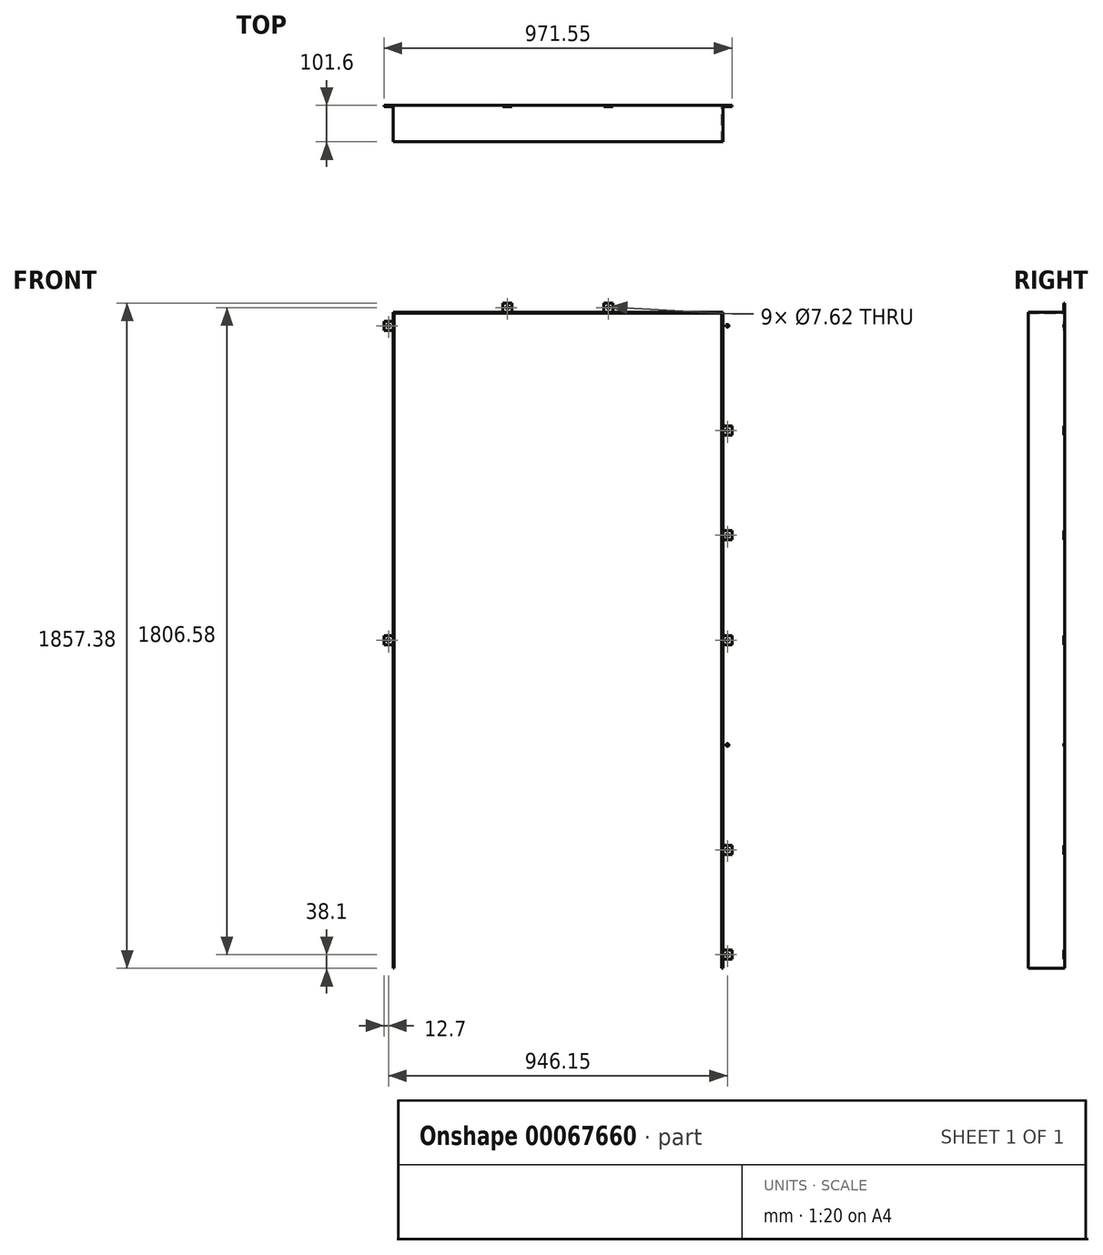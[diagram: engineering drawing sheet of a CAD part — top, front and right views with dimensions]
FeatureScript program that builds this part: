
annotation { "Feature Type Name" : "Feature", "Feature Type Description" : "" }
export const myFeature = defineFeature(function(context is Context, id is Id, definition is map)
    precondition{}
    {
        {
            var Q0;
            Q0=qCreatedBy(makeId("Front.planeOp"),FACE);
            var sketch = newSketch(context, id + "F0", { "sketchPlane" : qUnion([Q0])});
            skLineSegment(sketch, "E0", {"start": v(0, 0) * mm, "end": v(0, 1831.98) * mm});
            skLineSegment(sketch, "E1", {"start": v(0, 1831.98) * mm, "end": v(920.75, 1831.98) * mm});
            skLineSegment(sketch, "E2", {"start": v(920.75, 1831.98) * mm, "end": v(920.75, 0) * mm});
            skLineSegment(sketch, "E3", {"start": v(920.75, 0) * mm, "end": v(917.58, 0) * mm});
            skLineSegment(sketch, "E4", {"start": v(917.58, 0) * mm, "end": v(917.58, 1828.8) * mm});
            skLineSegment(sketch, "E5", {"start": v(917.58, 1828.8) * mm, "end": v(3.17, 1828.8) * mm});
            skLineSegment(sketch, "E6", {"start": v(3.18, 1828.8) * mm, "end": v(3.18, 0) * mm});
            skLineSegment(sketch, "E7", {"start": v(3.18, 0) * mm, "end": v(0, 0) * mm});
            skLineSegment(sketch, "E8", {"start": v(460.38, 1831.98) * mm, "end": v(460.38, 1828.8) * mm, "construction": true});
            skLineSegment(sketch, "E9", {"start": v(460.38, 1828.8) * mm, "end": v(460.38, -376.43) * mm, "construction": true});
            skLineSegment(sketch, "E10.bottom", {"start": v(0, 1806.57) * mm, "end": v(-25.4, 1806.57) * mm});
            skLineSegment(sketch, "E10.top", {"start": v(0, 1781.17) * mm, "end": v(-25.4, 1781.17) * mm});
            skLineSegment(sketch, "E10.left", {"start": v(0, 1806.57) * mm, "end": v(0, 1781.17) * mm});
            skLineSegment(sketch, "E10.right", {"start": v(-25.4, 1806.57) * mm, "end": v(-25.4, 1781.17) * mm});
            skLineSegment(sketch, "E11", {"start": v(-12.7, 1806.57) * mm, "end": v(-12.7, 1781.17) * mm, "construction": true});
            skLineSegment(sketch, "E12", {"start": v(-25.4, 1793.87) * mm, "end": v(0, 1793.87) * mm, "construction": true});
            skCircle(sketch, "E13", {"center": v(-12.7, 1793.87) * mm, "radius": 3.81 * mm});
            skLineSegment(sketch, "E14.left", {"start": v(0, 1513.95) * mm, "end": v(0, 1488.55) * mm});
            skLineSegment(sketch, "E15", {"start": v(-25.4, 1501.25) * mm, "end": v(0, 1501.25) * mm, "construction": true});
            skLineSegment(sketch, "E16", {"start": v(-12.7, 1513.95) * mm, "end": v(-12.7, 1488.55) * mm, "construction": true});
            skLineSegment(sketch, "E14.right", {"start": v(-25.4, 1513.95) * mm, "end": v(-25.4, 1488.55) * mm});
            skLineSegment(sketch, "E14.top", {"start": v(0, 1488.55) * mm, "end": v(-25.4, 1488.55) * mm});
            skLineSegment(sketch, "E14.bottom", {"start": v(0, 1513.95) * mm, "end": v(-25.4, 1513.95) * mm});
            skCircle(sketch, "E17", {"center": v(-12.7, 1501.25) * mm, "radius": 3.81 * mm});
            skLineSegment(sketch, "E18.left", {"start": v(0, 1221.32) * mm, "end": v(0, 1195.92) * mm});
            skLineSegment(sketch, "E19", {"start": v(-25.4, 1208.62) * mm, "end": v(0, 1208.62) * mm, "construction": true});
            skLineSegment(sketch, "E20", {"start": v(-12.7, 1221.32) * mm, "end": v(-12.7, 1195.92) * mm, "construction": true});
            skLineSegment(sketch, "E18.right", {"start": v(-25.4, 1221.32) * mm, "end": v(-25.4, 1195.92) * mm});
            skLineSegment(sketch, "E18.top", {"start": v(0, 1195.92) * mm, "end": v(-25.4, 1195.92) * mm});
            skLineSegment(sketch, "E18.bottom", {"start": v(0, 1221.32) * mm, "end": v(-25.4, 1221.32) * mm});
            skCircle(sketch, "E21", {"center": v(-12.7, 1208.62) * mm, "radius": 3.81 * mm});
            skLineSegment(sketch, "E22.left", {"start": v(0, 50.8) * mm, "end": v(0, 25.4) * mm});
            skLineSegment(sketch, "E23", {"start": v(-25.4, 38.1) * mm, "end": v(0, 38.1) * mm, "construction": true});
            skLineSegment(sketch, "E24", {"start": v(-12.7, 50.8) * mm, "end": v(-12.7, 25.4) * mm, "construction": true});
            skLineSegment(sketch, "E22.right", {"start": v(-25.4, 50.8) * mm, "end": v(-25.4, 25.4) * mm});
            skLineSegment(sketch, "E22.top", {"start": v(0, 25.4) * mm, "end": v(-25.4, 25.4) * mm});
            skLineSegment(sketch, "E22.bottom", {"start": v(0, 50.8) * mm, "end": v(-25.4, 50.8) * mm});
            skCircle(sketch, "E25", {"center": v(-12.7, 38.1) * mm, "radius": 3.81 * mm});
            skLineSegment(sketch, "E26.left", {"start": v(0, 343.43) * mm, "end": v(0, 318.03) * mm});
            skLineSegment(sketch, "E27", {"start": v(-25.4, 330.73) * mm, "end": v(0, 330.73) * mm, "construction": true});
            skLineSegment(sketch, "E28", {"start": v(-12.7, 343.43) * mm, "end": v(-12.7, 318.03) * mm, "construction": true});
            skLineSegment(sketch, "E26.right", {"start": v(-25.4, 343.43) * mm, "end": v(-25.4, 318.03) * mm});
            skLineSegment(sketch, "E26.top", {"start": v(0, 318.03) * mm, "end": v(-25.4, 318.03) * mm});
            skLineSegment(sketch, "E26.bottom", {"start": v(0, 343.43) * mm, "end": v(-25.4, 343.43) * mm});
            skCircle(sketch, "E29", {"center": v(-12.7, 330.73) * mm, "radius": 3.81 * mm});
            skLineSegment(sketch, "E30.left", {"start": v(0, 636.06) * mm, "end": v(0, 610.66) * mm});
            skLineSegment(sketch, "E31", {"start": v(-25.4, 623.36) * mm, "end": v(0, 623.36) * mm, "construction": true});
            skLineSegment(sketch, "E32", {"start": v(-12.7, 636.06) * mm, "end": v(-12.7, 610.66) * mm, "construction": true});
            skLineSegment(sketch, "E30.right", {"start": v(-25.4, 636.06) * mm, "end": v(-25.4, 610.66) * mm});
            skLineSegment(sketch, "E30.top", {"start": v(0, 610.66) * mm, "end": v(-25.4, 610.66) * mm});
            skLineSegment(sketch, "E30.bottom", {"start": v(0, 636.06) * mm, "end": v(-25.4, 636.06) * mm});
            skCircle(sketch, "E33", {"center": v(-12.7, 623.36) * mm, "radius": 3.81 * mm});
            skLineSegment(sketch, "E34.MirrorCS", {"start": v(946.15, 1793.87) * mm, "end": v(920.75, 1793.87) * mm, "construction": true});
            skCircle(sketch, "E35.MirrorC", {"center": v(933.45, 1793.88) * mm, "radius": 3.81 * mm});
            skLineSegment(sketch, "E36.MirrorCS", {"start": v(920.75, 1806.57) * mm, "end": v(946.15, 1806.57) * mm});
            skLineSegment(sketch, "E37.MirrorCS", {"start": v(933.45, 1806.58) * mm, "end": v(933.45, 1781.18) * mm, "construction": true});
            skLineSegment(sketch, "E38.MirrorCS", {"start": v(946.15, 1806.58) * mm, "end": v(946.15, 1781.18) * mm});
            skLineSegment(sketch, "E39.MirrorCS", {"start": v(920.75, 1806.58) * mm, "end": v(920.75, 1781.18) * mm});
            skLineSegment(sketch, "E40.MirrorCS", {"start": v(920.75, 1781.17) * mm, "end": v(946.15, 1781.17) * mm});
            skLineSegment(sketch, "E41.MirrorCS", {"start": v(946.15, 1501.25) * mm, "end": v(920.75, 1501.25) * mm, "construction": true});
            skLineSegment(sketch, "E42.MirrorCS", {"start": v(920.75, 1513.95) * mm, "end": v(946.15, 1513.95) * mm});
            skCircle(sketch, "E43.MirrorC", {"center": v(933.45, 1501.25) * mm, "radius": 3.81 * mm});
            skLineSegment(sketch, "E44.MirrorCS", {"start": v(920.75, 1513.95) * mm, "end": v(920.75, 1488.55) * mm});
            skLineSegment(sketch, "E45.MirrorCS", {"start": v(933.45, 1513.95) * mm, "end": v(933.45, 1488.55) * mm, "construction": true});
            skLineSegment(sketch, "E46.MirrorCS", {"start": v(946.15, 1513.95) * mm, "end": v(946.15, 1488.55) * mm});
            skLineSegment(sketch, "E47.MirrorCS", {"start": v(920.75, 1488.55) * mm, "end": v(946.15, 1488.55) * mm});
            skLineSegment(sketch, "E48.MirrorCS", {"start": v(946.15, 1221.32) * mm, "end": v(946.15, 1195.92) * mm});
            skLineSegment(sketch, "E49.MirrorCS", {"start": v(946.15, 1208.62) * mm, "end": v(920.75, 1208.62) * mm, "construction": true});
            skLineSegment(sketch, "E50.MirrorCS", {"start": v(933.45, 1221.32) * mm, "end": v(933.45, 1195.92) * mm, "construction": true});
            skCircle(sketch, "E51.MirrorC", {"center": v(933.45, 1208.62) * mm, "radius": 3.81 * mm});
            skLineSegment(sketch, "E52.MirrorCS", {"start": v(920.75, 1195.92) * mm, "end": v(946.15, 1195.92) * mm});
            skLineSegment(sketch, "E53.MirrorCS", {"start": v(920.75, 1221.32) * mm, "end": v(920.75, 1195.92) * mm});
            skLineSegment(sketch, "E54.MirrorCS", {"start": v(920.75, 1221.32) * mm, "end": v(946.15, 1221.32) * mm});
            skCircle(sketch, "E55.MirrorC", {"center": v(933.45, 623.36) * mm, "radius": 3.81 * mm});
            skLineSegment(sketch, "E56.MirrorCS", {"start": v(920.75, 636.06) * mm, "end": v(946.15, 636.06) * mm});
            skLineSegment(sketch, "E57.MirrorCS", {"start": v(946.15, 623.36) * mm, "end": v(920.75, 623.36) * mm, "construction": true});
            skLineSegment(sketch, "E58.MirrorCS", {"start": v(933.45, 636.06) * mm, "end": v(933.45, 610.66) * mm, "construction": true});
            skLineSegment(sketch, "E59.MirrorCS", {"start": v(920.75, 636.06) * mm, "end": v(920.75, 610.66) * mm});
            skLineSegment(sketch, "E60.MirrorCS", {"start": v(920.75, 610.66) * mm, "end": v(946.15, 610.66) * mm});
            skLineSegment(sketch, "E61.MirrorCS", {"start": v(946.15, 636.06) * mm, "end": v(946.15, 610.66) * mm});
            skLineSegment(sketch, "E62.MirrorCS", {"start": v(946.15, 343.43) * mm, "end": v(946.15, 318.03) * mm});
            skLineSegment(sketch, "E63.MirrorCS", {"start": v(920.75, 318.03) * mm, "end": v(946.15, 318.03) * mm});
            skLineSegment(sketch, "E64.MirrorCS", {"start": v(933.45, 343.43) * mm, "end": v(933.45, 318.03) * mm, "construction": true});
            skLineSegment(sketch, "E65.MirrorCS", {"start": v(920.75, 343.43) * mm, "end": v(946.15, 343.43) * mm});
            skLineSegment(sketch, "E66.MirrorCS", {"start": v(946.15, 330.73) * mm, "end": v(920.75, 330.73) * mm, "construction": true});
            skLineSegment(sketch, "E67.MirrorCS", {"start": v(920.75, 343.43) * mm, "end": v(920.75, 318.03) * mm});
            skCircle(sketch, "E68.MirrorC", {"center": v(933.45, 330.73) * mm, "radius": 3.81 * mm});
            skLineSegment(sketch, "E69.MirrorCS", {"start": v(946.15, 50.8) * mm, "end": v(946.15, 25.4) * mm});
            skLineSegment(sketch, "E70.MirrorCS", {"start": v(933.45, 50.8) * mm, "end": v(933.45, 25.4) * mm, "construction": true});
            skLineSegment(sketch, "E71.MirrorCS", {"start": v(946.15, 38.1) * mm, "end": v(920.75, 38.1) * mm, "construction": true});
            skCircle(sketch, "E72.MirrorC", {"center": v(933.45, 38.1) * mm, "radius": 3.81 * mm});
            skLineSegment(sketch, "E73.MirrorCS", {"start": v(920.75, 50.8) * mm, "end": v(946.15, 50.8) * mm});
            skLineSegment(sketch, "E74.MirrorCS", {"start": v(920.75, 50.8) * mm, "end": v(920.75, 25.4) * mm});
            skLineSegment(sketch, "E75.MirrorCS", {"start": v(920.75, 25.4) * mm, "end": v(946.15, 25.4) * mm});
            skLineSegment(sketch, "E76.bottom", {"start": v(25.4, 1831.98) * mm, "end": v(50.8, 1831.98) * mm});
            skLineSegment(sketch, "E76.top", {"start": v(25.4, 1857.38) * mm, "end": v(50.8, 1857.38) * mm});
            skLineSegment(sketch, "E76.left", {"start": v(25.4, 1831.98) * mm, "end": v(25.4, 1857.38) * mm});
            skLineSegment(sketch, "E76.right", {"start": v(50.8, 1831.98) * mm, "end": v(50.8, 1857.38) * mm});
            skLineSegment(sketch, "E77.bottom", {"start": v(895.35, 1831.98) * mm, "end": v(869.95, 1831.98) * mm});
            skLineSegment(sketch, "E77.top", {"start": v(895.35, 1857.38) * mm, "end": v(869.95, 1857.38) * mm});
            skLineSegment(sketch, "E77.left", {"start": v(895.35, 1831.98) * mm, "end": v(895.35, 1857.38) * mm});
            skLineSegment(sketch, "E77.right", {"start": v(869.95, 1831.98) * mm, "end": v(869.95, 1857.38) * mm});
            skLineSegment(sketch, "E78", {"start": v(869.95, 1857.38) * mm, "end": v(895.35, 1831.98) * mm, "construction": true});
            skLineSegment(sketch, "E79", {"start": v(895.35, 1857.38) * mm, "end": v(869.95, 1831.98) * mm, "construction": true});
            skCircle(sketch, "E80", {"center": v(882.65, 1844.68) * mm, "radius": 3.81 * mm});
            skLineSegment(sketch, "E81", {"start": v(25.4, 1857.38) * mm, "end": v(50.8, 1831.98) * mm, "construction": true});
            skLineSegment(sketch, "E82", {"start": v(50.8, 1857.38) * mm, "end": v(25.4, 1831.98) * mm, "construction": true});
            skCircle(sketch, "E83", {"center": v(38.1, 1844.68) * mm, "radius": 3.81 * mm});
            skLineSegment(sketch, "E84", {"start": v(306.92, 1844.68) * mm, "end": v(332.32, 1844.68) * mm, "construction": true});
            skCircle(sketch, "E85", {"center": v(319.62, 1844.68) * mm, "radius": 3.81 * mm});
            skLineSegment(sketch, "E86.left", {"start": v(332.32, 1857.38) * mm, "end": v(332.32, 1831.98) * mm});
            skLineSegment(sketch, "E86.top", {"start": v(332.32, 1831.98) * mm, "end": v(306.92, 1831.98) * mm});
            skLineSegment(sketch, "E86.bottom", {"start": v(332.32, 1857.38) * mm, "end": v(306.92, 1857.38) * mm});
            skLineSegment(sketch, "E87", {"start": v(319.62, 1857.38) * mm, "end": v(319.62, 1831.98) * mm, "construction": true});
            skLineSegment(sketch, "E86.right", {"start": v(306.92, 1857.38) * mm, "end": v(306.92, 1831.98) * mm});
            skLineSegment(sketch, "E88", {"start": v(588.43, 1844.67) * mm, "end": v(613.83, 1844.67) * mm, "construction": true});
            skCircle(sketch, "E89", {"center": v(601.13, 1844.68) * mm, "radius": 3.81 * mm});
            skLineSegment(sketch, "E90.left", {"start": v(613.83, 1857.38) * mm, "end": v(613.83, 1831.98) * mm});
            skLineSegment(sketch, "E90.top", {"start": v(613.83, 1831.98) * mm, "end": v(588.43, 1831.98) * mm});
            skLineSegment(sketch, "E90.bottom", {"start": v(613.83, 1857.38) * mm, "end": v(588.43, 1857.38) * mm});
            skLineSegment(sketch, "E91", {"start": v(601.13, 1857.38) * mm, "end": v(601.13, 1831.98) * mm, "construction": true});
            skLineSegment(sketch, "E90.right", {"start": v(588.43, 1857.38) * mm, "end": v(588.43, 1831.98) * mm});
            skLineSegment(sketch, "E92.top", {"start": v(0, 903.29) * mm, "end": v(-25.4, 903.29) * mm});
            skLineSegment(sketch, "E93", {"start": v(-12.7, 928.69) * mm, "end": v(-12.7, 903.29) * mm, "construction": true});
            skCircle(sketch, "E94", {"center": v(-12.7, 915.99) * mm, "radius": 3.81 * mm});
            skLineSegment(sketch, "E95", {"start": v(-25.4, 915.99) * mm, "end": v(0, 915.99) * mm, "construction": true});
            skLineSegment(sketch, "E92.left", {"start": v(0, 928.69) * mm, "end": v(0, 903.29) * mm});
            skLineSegment(sketch, "E92.bottom", {"start": v(0, 928.69) * mm, "end": v(-25.4, 928.69) * mm});
            skLineSegment(sketch, "E92.right", {"start": v(-25.4, 928.69) * mm, "end": v(-25.4, 903.29) * mm});
            skLineSegment(sketch, "E96", {"start": v(-12.7, 38.1) * mm, "end": v(-12.7, 330.73) * mm, "construction": true});
            skLineSegment(sketch, "E97", {"start": v(-12.7, 330.73) * mm, "end": v(-12.7, 623.36) * mm, "construction": true});
            skLineSegment(sketch, "E98", {"start": v(-12.7, 623.36) * mm, "end": v(-12.7, 915.99) * mm, "construction": true});
            skLineSegment(sketch, "E99", {"start": v(-12.7, 915.99) * mm, "end": v(-12.7, 1208.62) * mm, "construction": true});
            skLineSegment(sketch, "E100", {"start": v(-12.7, 1208.62) * mm, "end": v(-12.7, 1501.25) * mm, "construction": true});
            skLineSegment(sketch, "E101", {"start": v(-12.7, 1793.87) * mm, "end": v(-12.7, 1501.25) * mm, "construction": true});
            skLineSegment(sketch, "E102.MirrorCS", {"start": v(933.45, 928.69) * mm, "end": v(933.45, 903.29) * mm, "construction": true});
            skLineSegment(sketch, "E103.MirrorCS", {"start": v(946.15, 915.99) * mm, "end": v(920.75, 915.99) * mm, "construction": true});
            skLineSegment(sketch, "E104.MirrorCS", {"start": v(920.75, 928.69) * mm, "end": v(946.15, 928.69) * mm});
            skCircle(sketch, "E105.MirrorC", {"center": v(933.45, 915.99) * mm, "radius": 3.81 * mm});
            skLineSegment(sketch, "E106.MirrorCS", {"start": v(920.75, 903.29) * mm, "end": v(946.15, 903.29) * mm});
            skLineSegment(sketch, "E107.MirrorCS", {"start": v(946.15, 928.69) * mm, "end": v(946.15, 903.29) * mm});
            skLineSegment(sketch, "E108.MirrorCS", {"start": v(920.75, 928.69) * mm, "end": v(920.75, 903.29) * mm});
            skLineSegment(sketch, "E109", {"start": v(38.1, 1844.67) * mm, "end": v(319.62, 1844.68) * mm, "construction": true});
            skLineSegment(sketch, "E110", {"start": v(601.13, 1844.67) * mm, "end": v(882.65, 1844.67) * mm, "construction": true});
            skLineSegment(sketch, "E111", {"start": v(319.62, 1844.67) * mm, "end": v(601.13, 1844.67) * mm, "construction": true});
            skSolve(sketch);
        }
        {
            var Q0;
            {var subQ15=sQuery(id+"F0.wireOp",EDGE,"E1");Q0=makeQuery(id+"F0.imprint","IMPRINT",FACE,{"disambiguationData":[TD([[makeQuery(id+"F0.imprint","IMPRINT",EDGE,{"derivedFrom":subQ15}),-1.0]])]});}
            extrude(context, id + "F1", {"entities" : qUnion([Q0]), "depth" : 101.6 * mm});
        }
        {
            var Q0;
            Q0=makeQuery(id+"F0.imprint","IMPRINT",FACE,{"disambiguationData":[TD([[makeQuery(id+"F0.imprint","IMPRINT",EDGE,{"derivedFrom":sQuery(id+"F0.wireOp",EDGE,"E69.MirrorCS")}),-1.0]])]});
            var Q1;
            Q1=makeQuery(id+"F0.imprint","IMPRINT",FACE,{"disambiguationData":[TD([[makeQuery(id+"F0.imprint","IMPRINT",EDGE,{"derivedFrom":sQuery(id+"F0.wireOp",EDGE,"E62.MirrorCS")}),-1.0]])]});
            var Q2;
            Q2=makeQuery(id+"F0.imprint","IMPRINT",FACE,{"disambiguationData":[TD([[makeQuery(id+"F0.imprint","IMPRINT",EDGE,{"derivedFrom":sQuery(id+"F0.wireOp",EDGE,"E55.MirrorC")}),1.0]])]});
            var Q3;
            Q3=makeQuery(id+"F0.imprint","IMPRINT",FACE,{"disambiguationData":[TD([[makeQuery(id+"F0.imprint","IMPRINT",EDGE,{"derivedFrom":sQuery(id+"F0.wireOp",EDGE,"E48.MirrorCS")}),-1.0]])]});
            var Q4;
            Q4=makeQuery(id+"F0.imprint","IMPRINT",FACE,{"disambiguationData":[TD([[makeQuery(id+"F0.imprint","IMPRINT",EDGE,{"derivedFrom":sQuery(id+"F0.wireOp",EDGE,"E42.MirrorCS")}),-1.0]])]});
            var Q5;
            Q5=makeQuery(id+"F0.imprint","IMPRINT",FACE,{"disambiguationData":[TD([[makeQuery(id+"F0.imprint","IMPRINT",EDGE,{"derivedFrom":sQuery(id+"F0.wireOp",EDGE,"E35.MirrorC")}),1.0]])]});
            var Q6;
            Q6=makeQuery(id+"F0.imprint","IMPRINT",FACE,{"disambiguationData":[TD([[makeQuery(id+"F0.imprint","IMPRINT",EDGE,{"derivedFrom":sQuery(id+"F0.wireOp",EDGE,"E10.bottom")}),1.0]])]});
            var Q7;
            Q7=makeQuery(id+"F0.imprint","IMPRINT",FACE,{"disambiguationData":[TD([[makeQuery(id+"F0.imprint","IMPRINT",EDGE,{"derivedFrom":sQuery(id+"F0.wireOp",EDGE,"E14.left")}),-1.0]])]});
            var Q8;
            Q8=makeQuery(id+"F0.imprint","IMPRINT",FACE,{"disambiguationData":[TD([[makeQuery(id+"F0.imprint","IMPRINT",EDGE,{"derivedFrom":sQuery(id+"F0.wireOp",EDGE,"E18.left")}),-1.0]])]});
            var Q9;
            Q9=makeQuery(id+"F0.imprint","IMPRINT",FACE,{"disambiguationData":[TD([[makeQuery(id+"F0.imprint","IMPRINT",EDGE,{"derivedFrom":sQuery(id+"F0.wireOp",EDGE,"E30.left")}),-1.0]])]});
            var Q10;
            Q10=makeQuery(id+"F0.imprint","IMPRINT",FACE,{"disambiguationData":[TD([[makeQuery(id+"F0.imprint","IMPRINT",EDGE,{"derivedFrom":sQuery(id+"F0.wireOp",EDGE,"E26.left")}),-1.0]])]});
            var Q11;
            Q11=makeQuery(id+"F0.imprint","IMPRINT",FACE,{"disambiguationData":[TD([[makeQuery(id+"F0.imprint","IMPRINT",EDGE,{"derivedFrom":sQuery(id+"F0.wireOp",EDGE,"E22.left")}),-1.0]])]});
            var Q12;
            Q12=makeQuery(id+"F0.imprint","IMPRINT",FACE,{"disambiguationData":[TD([[makeQuery(id+"F0.imprint","IMPRINT",EDGE,{"derivedFrom":sQuery(id+"F0.wireOp",EDGE,"E76.bottom")}),1.0]])]});
            var Q13;
            Q13=makeQuery(id+"F0.imprint","IMPRINT",FACE,{"disambiguationData":[TD([[makeQuery(id+"F0.imprint","IMPRINT",EDGE,{"derivedFrom":sQuery(id+"F0.wireOp",EDGE,"e8b36b14-baf5-47ac-a38b-4cfdd02c8466.bottom")}),1.0]])]});
            var Q14;
            Q14=makeQuery(id+"F0.imprint","IMPRINT",FACE,{"disambiguationData":[TD([[makeQuery(id+"F0.imprint","IMPRINT",EDGE,{"derivedFrom":sQuery(id+"F0.wireOp",EDGE,"E77.bottom")}),-1.0]])]});
            var Q15;
            Q15=makeQuery(id+"F0.imprint","IMPRINT",FACE,{"disambiguationData":[TD([[makeQuery(id+"F0.imprint","IMPRINT",EDGE,{"derivedFrom":sQuery(id+"F0.wireOp",EDGE,"E85")}),-1.0]])]});
            var Q16;
            Q16=makeQuery(id+"F0.imprint","IMPRINT",FACE,{"disambiguationData":[TD([[makeQuery(id+"F0.imprint","IMPRINT",EDGE,{"derivedFrom":sQuery(id+"F0.wireOp",EDGE,"70c7b6a7-01ed-414b-a764-cb33e45972b0")}),-1.0]])]});
            var Q17;
            Q17=makeQuery(id+"F0.imprint","IMPRINT",FACE,{"disambiguationData":[TD([[makeQuery(id+"F0.imprint","IMPRINT",EDGE,{"derivedFrom":sQuery(id+"F0.wireOp",EDGE,"edc6d6db-5635-4a53-b6f9-896006902fa9")}),-1.0]])]});
            var Q18;
            Q18=makeQuery(id+"F0.imprint","IMPRINT",FACE,{"disambiguationData":[TD([[makeQuery(id+"F0.imprint","IMPRINT",EDGE,{"derivedFrom":sQuery(id+"F0.wireOp",EDGE,"E89")}),-1.0]])]});
            var Q19;
            Q19=makeQuery(id+"F0.imprint","IMPRINT",FACE,{"disambiguationData":[TD([[makeQuery(id+"F0.imprint","IMPRINT",EDGE,{"derivedFrom":sQuery(id+"F0.wireOp",EDGE,"E92.top")}),-1.0]])]});
            var Q20;
            Q20=makeQuery(id+"F0.imprint","IMPRINT",FACE,{"disambiguationData":[TD([[makeQuery(id+"F0.imprint","IMPRINT",EDGE,{"derivedFrom":sQuery(id+"F0.wireOp",EDGE,"E106.MirrorCS")}),1.0]])]});
            extrude(context, id + "F2", {"entities" : qUnion([Q0, Q1, Q2, Q3, Q4, Q5, Q6, Q7, Q8, Q9, Q10, Q11, Q12, Q13, Q14, Q15, Q16, Q17, Q18, Q19, Q20]), "operationType" : NewBodyOperationType.ADD, "depth" : 3.17 * mm});
        }
    });
